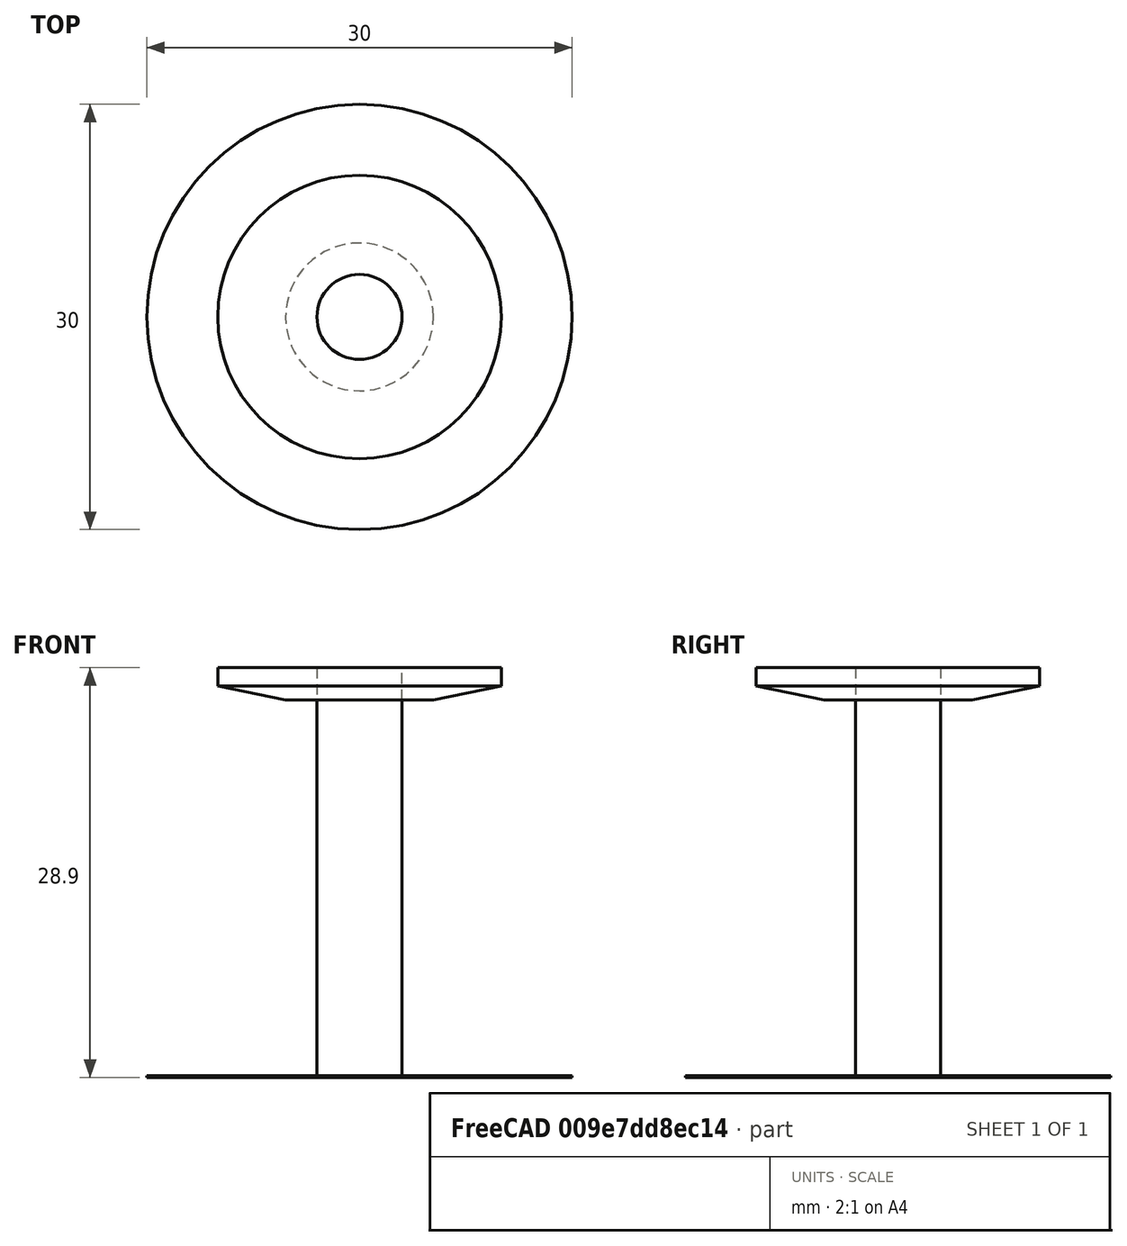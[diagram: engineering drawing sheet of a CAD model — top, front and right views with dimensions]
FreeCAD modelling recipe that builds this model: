
FCSTD DOCUMENT  (FreeCAD 0.17R9747 (Git))
Label: RM3
License: All rights reserved
LicenseURL: http://en.wikipedia.org/wiki/All_rights_reserved
objects: Part::Cylinder×3, Mesh::Feature×2, Part::Cut×2, Part::MultiFuse×1, Sketcher::SketchObject×1, Part::Revolution×1
note: 8 computed .brp shape members not serialized (recipe doc carries the construction recipe); baked Part::Feature solids carry a one-line shape summary decoded from their .brp

FEATURE [Mesh::Feature] float  label="float_stl"
FEATURE [Mesh::Feature] plate  label="spar_stl"
  Placement = pos=(0,0,-20.19) rot=(0,0,1;0rad)
  expr: Placement.Base.z = 8.7100000000000009 - 28.899989999999999
FEATURE [Part::Cylinder] Cylinder
  Angle = 360
  AttacherType = Attacher::AttachEngine3D
  Height = 10
  Radius = 15
FEATURE [Part::Cylinder] Cylinder001
  Angle = 360
  AttacherType = Attacher::AttachEngine3D
  Height = 37.95
  Placement = pos=(0,0,-28.8499) rot=(0,0,1;0rad)
  Radius = 3
  expr: Height = 38 - 0.050000000000000003
  expr: Placement.Base.z = -28.899899999999999 + 0.050000000000000003
FEATURE [Part::Cylinder] Cylinder002
  Angle = 360
  AttacherType = Attacher::AttachEngine3D
  Height = 0.1
  Placement = pos=(0,0,-28.9) rot=(0,0,1;0rad)
  Radius = 15
FEATURE [Part::MultiFuse] Fusion  label="spar"
  Shapes = -> [Cylinder002,Cylinder001]
FEATURE [Part::Cut] Cut001  label="cut_spar"
  Base = -> Fusion
  Tool = -> Cylinder
FEATURE [Sketcher::SketchObject] Sketch
  Placement = pos=(0,0,0) rot=(-1,0,0;4.71239rad)
  sketch-geometry (5):
    g0: LineSegment StartX=-3 StartY=0 StartZ=0 EndX=-5.21369 EndY=0 EndZ=0
    g1: LineSegment StartX=-5.21369 StartY=0 StartZ=0 EndX=-10 EndY=1 EndZ=0
    g2: LineSegment StartX=-10 StartY=1 StartZ=0 EndX=-10 EndY=5 EndZ=0
    g3: LineSegment StartX=-10 StartY=5 StartZ=0 EndX=-3 EndY=5 EndZ=0
    g4: LineSegment StartX=-3 StartY=5 StartZ=0 EndX=-3 EndY=0 EndZ=0
  constraints (14):
    c: Horizontal(g0)
    c: Coincident(g0,g1)
    c: Coincident(g1,g2)
    c: Vertical(g2)
    c: Coincident(g2,g3)
    c: Horizontal(g3)
    c: Coincident(g3,g4)
    c: Coincident(g4,g0)
    c: Vertical(g4)
    c: DistanceX(g3,g-1) = 3
    c: DistanceX(g2,g-1) = 10
    c: Distance(g4) = 5
    c: Distance(g2) = 4
    c: DistanceY(g0,g-1) = 0
FEATURE [Part::Revolution] Revolve  label="float"
  Angle = 360
  Axis = (0,0,1)
  Base = (0,0,0)
  FaceMakerClass = Part::FaceMakerBullseye
  Placement = pos=(0,0,-2.28) rot=(0,0,1;0rad)
  Solid = true
  Source = -> Sketch
  Symmetric = false
FEATURE [Part::Cut] Cut  label="cut_float"
  Base = -> Revolve
  Tool = -> Cylinder
